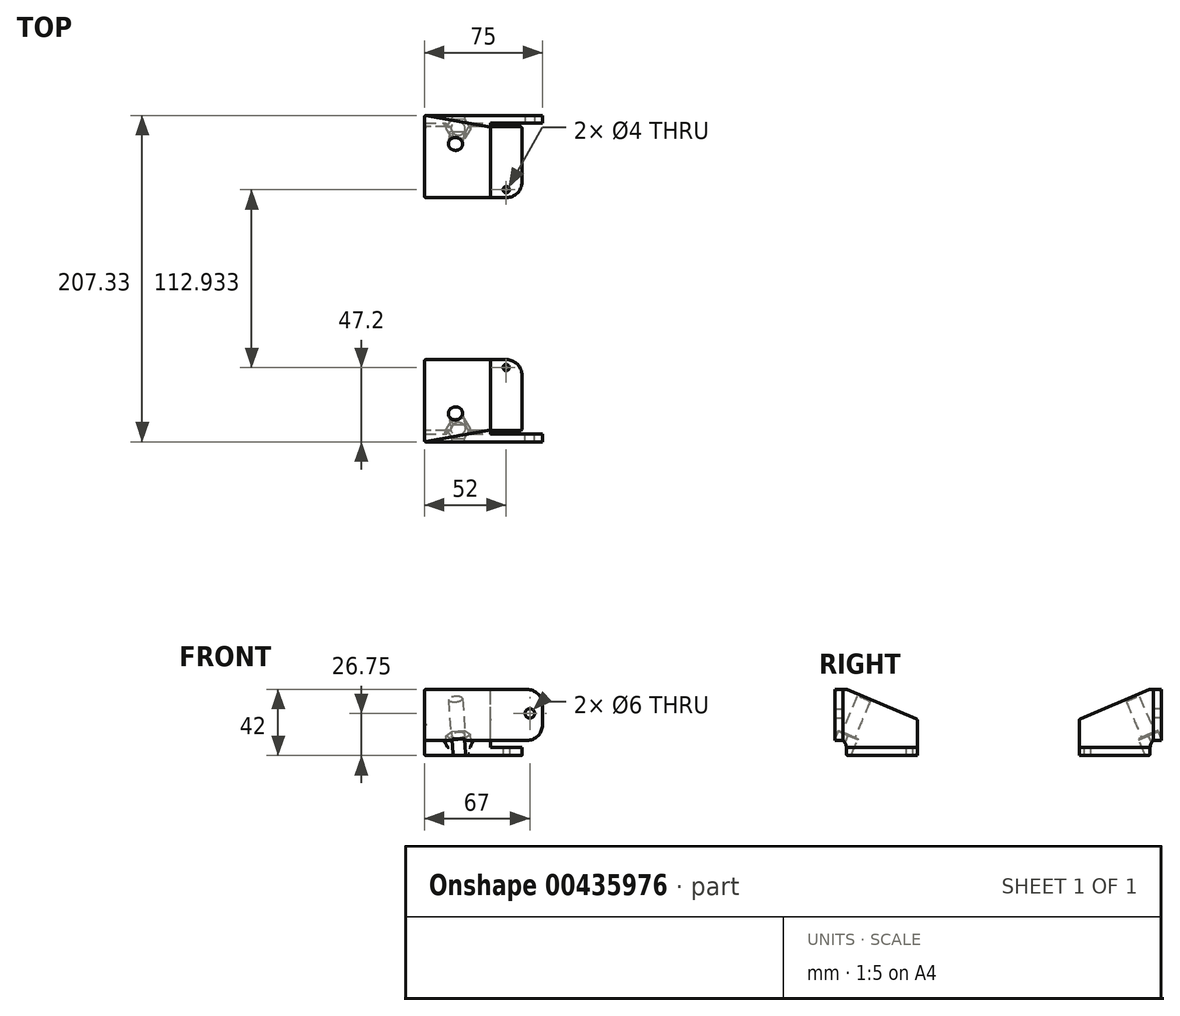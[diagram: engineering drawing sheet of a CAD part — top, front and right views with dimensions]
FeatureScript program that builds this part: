
annotation { "Feature Type Name" : "Feature", "Feature Type Description" : "" }
export const myFeature = defineFeature(function(context is Context, id is Id, definition is map)
    precondition{}
    {
        {
            var Q0;
            Q0=qCreatedBy(makeId("Top.planeOp"),FACE);
            var sketch = newSketch(context, id + "F0", { "sketchPlane" : qUnion([Q0])});
            skLineSegment(sketch, "E0.bottom", {"start": v(10, -22.5) * mm, "end": v(-10, -22.5) * mm});
            skLineSegment(sketch, "E0.top", {"start": v(10, 22.5) * mm, "end": v(-10, 22.5) * mm});
            skLineSegment(sketch, "E0.left", {"start": v(10, -22.5) * mm, "end": v(10, 22.5) * mm});
            skLineSegment(sketch, "E0.right", {"start": v(-10, -22.5) * mm, "end": v(-10, 22.5) * mm});
            skPoint(sketch, "E0.middle", {"position": v(0, 0) * mm});
            skCircle(sketch, "E1", {"center": v(0, 17.5) * mm, "radius": 2 * mm});
            skSolve(sketch);
        }
        {
            var Q0;
            Q0=makeQuery(id+"F0.imprint","IMPRINT",FACE,{"disambiguationData":[TD([[makeQuery(id+"F0.imprint","IMPRINT",EDGE,{"derivedFrom":sQuery(id+"F0.wireOp",EDGE,"E0.bottom")}),-1.0]])]});
            extrude(context, id + "F1", {"entities" : qUnion([Q0]), "depth" : 5 * mm});
        }
        {
            var Q0;
            Q0=makeQuery(id+"F1.opExtrude","SWEPT_FACE",FACE,{"disambiguationData":[OSD([sQuery(id+"F0.wireOp",EDGE,"E0.right")])]});
            var sketch = newSketch(context, id + "F2", { "sketchPlane" : qUnion([Q0])});
            skPoint(sketch, "E2.0", {"position": v(-22.5, 0) * mm});
            skLineSegment(sketch, "E3.bottom", {"start": v(-22.5, 0) * mm, "end": v(22.5, 0) * mm});
            skLineSegment(sketch, "E3.top", {"start": v(-22.5, 42) * mm, "end": v(22.5, 42) * mm});
            skLineSegment(sketch, "E3.left", {"start": v(-22.5, 0) * mm, "end": v(-22.5, 42) * mm});
            skLineSegment(sketch, "E3.right", {"start": v(22.5, 0) * mm, "end": v(22.5, 42) * mm});
            skSolve(sketch);
        }
        {
            var Q0;
            {var subQ0=sQuery(id+"F2.wireOp",EDGE,"E3.top");Q0=makeQuery(id+"F2.imprint","IMPRINT",FACE,{"disambiguationData":[TD([[makeQuery(id+"F2.imprint","IMPRINT",EDGE,{"derivedFrom":subQ0}),-1.0]])]});}
            var Q1;
            {var subQ0=sQuery(id+"F2.wireOp",EDGE,"E3.bottom");Q1=makeQuery(id+"F2.imprint","IMPRINT",FACE,{"disambiguationData":[TD([[makeQuery(id+"F2.imprint","IMPRINT",EDGE,{"derivedFrom":subQ0}),-1.0]])]});}
            extrude(context, id + "F3", {"entities" : qUnion([Q0, Q1]), "operationType" : NewBodyOperationType.ADD, "depth" : 42 * mm});
        }
        {
            var Q0;
            Q0=makeQuery(id+"F3.boolean.opBoolean","MERGE",FACE,{"derivedFrom":[makeQuery(id+"F1.opExtrude","SWEPT_FACE",FACE,{"disambiguationData":[OSD([sQuery(id+"F0.wireOp",EDGE,"E0.bottom")])]}),makeQuery(id+"F3.opExtrude","SWEPT_FACE",FACE,{"disambiguationData":[OSD([sQuery(id+"F2.wireOp",EDGE,"E3.right")])]})]});
            var sketch = newSketch(context, id + "F4", { "sketchPlane" : qUnion([Q0])});
            skPoint(sketch, "E4.0", {"position": v(-10, 5) * mm});
            skLineSegment(sketch, "E5.bottom", {"start": v(-10, 5) * mm, "end": v(-52, 5) * mm});
            skLineSegment(sketch, "E5.top", {"start": v(-10, 42) * mm, "end": v(-52, 42) * mm});
            skLineSegment(sketch, "E5.left", {"start": v(-10, 5) * mm, "end": v(-10, 42) * mm});
            skLineSegment(sketch, "E5.right", {"start": v(-52, 5) * mm, "end": v(-52, 42) * mm});
            skSolve(sketch);
        }
        {
            var Q0;
            Q0=makeQuery(id+"F4.imprint","IMPRINT",FACE,{"disambiguationData":[TD([[makeQuery(id+"F4.imprint","IMPRINT",EDGE,{"derivedFrom":sQuery(id+"F4.wireOp",EDGE,"E5.bottom")}),-1.0]])]});
            extrude(context, id + "F5", {"entities" : qUnion([Q0]), "operationType" : NewBodyOperationType.ADD, "depth" : 2.2 * mm});
        }
        {
            var Q0;
            Q0=makeQuery(id+"F5.opExtrude","CAP_FACE",FACE,{"disambiguationData":[OSD([sQuery(id+"F4.wireOp",EDGE,"E5.bottom"),sQuery(id+"F4.wireOp",EDGE,"E5.top"),sQuery(id+"F4.wireOp",EDGE,"E5.left"),sQuery(id+"F4.wireOp",EDGE,"E5.right")])],"isStart":false});
            var sketch = newSketch(context, id + "F6", { "sketchPlane" : qUnion([Q0])});
            skPoint(sketch, "E6.0", {"position": v(-10, 5) * mm});
            skPoint(sketch, "E7.0", {"position": v(-52, 42) * mm});
            skPoint(sketch, "E8.0", {"position": v(10, 5) * mm});
            skLineSegment(sketch, "E9.bottom", {"start": v(-52, 42) * mm, "end": v(23, 42) * mm});
            skLineSegment(sketch, "E9.top", {"start": v(-52, 9.55) * mm, "end": v(23, 9.55) * mm});
            skLineSegment(sketch, "E9.left", {"start": v(-52, 42) * mm, "end": v(-52, 9.55) * mm});
            skLineSegment(sketch, "E9.right", {"start": v(23, 42) * mm, "end": v(23, 9.55) * mm});
            skLineSegment(sketch, "E10", {"start": v(15, 9.55) * mm, "end": v(15, 42) * mm, "construction": true});
            skLineSegment(sketch, "E11", {"start": v(-10, 5) * mm, "end": v(-10, 26.75) * mm, "construction": true});
            skCircle(sketch, "E12", {"center": v(15, 26.75) * mm, "radius": 3 * mm});
            skSolve(sketch);
        }
        {
            var Q0;
            {var subQ3=sQuery(id+"F6.wireOp",EDGE,"E9.left");Q0=makeQuery(id+"F6.imprint","IMPRINT",FACE,{"disambiguationData":[TD([[makeQuery(id+"F6.imprint","IMPRINT",EDGE,{"derivedFrom":subQ3}),-1.0]])]});}
            var Q1;
            {var subQ3=sQuery(id+"F6.wireOp",EDGE,"E9.right");Q1=makeQuery(id+"F6.imprint","IMPRINT",FACE,{"disambiguationData":[TD([[makeQuery(id+"F6.imprint","IMPRINT",EDGE,{"derivedFrom":subQ3}),-1.0]])]});}
            extrude(context, id + "F7", {"entities" : qUnion([Q0, Q1]), "operationType" : NewBodyOperationType.ADD, "depth" : 5 * mm});
        }
        {
            var Q0;
            Q0=qCreatedBy(makeId("Right.planeOp"),FACE);
            var sketch = newSketch(context, id + "F8", { "sketchPlane" : qUnion([Q0])});
            skLineSegment(sketch, "E13", {"start": v(0, 0) * mm, "end": v(-80.94, 34.36) * mm, "construction": true});
            skSolve(sketch);
        }
        {
            var Q0;
            Q0=sQuery(id+"F8.wireOp",EDGE,"E13");
            cPlane(context, id + "F9", {"entities" : qUnion([Q0]), "cplaneType" : CPlaneType.LINE_ANGLE, "offset" : 25 * mm, "angle" : 0 * degree, "width" : 150 * mm, "height" : 150 * mm});
        }
        {
            var Q0;
            Q0=qCreatedBy(id+"F9.planeOp",FACE);
            var sketch = newSketch(context, id + "F10", { "sketchPlane" : qUnion([Q0])});
            skLineSegment(sketch, "E14", {"start": v(-52.7, -8.91) * mm, "end": v(-52.7, 97.33) * mm, "construction": true});
            skSolve(sketch);
        }
        {
            var Q0;
            Q0=sQuery(id+"F10.wireOp",EDGE,"E14");
            cPlane(context, id + "F11", {"entities" : qUnion([Q0]), "cplaneType" : CPlaneType.LINE_ANGLE, "offset" : 25 * mm, "angle" : 4 * degree, "width" : 150 * mm, "height" : 150 * mm});
        }
        {
            var Q0;
            Q0=qCreatedBy(id+"F11.planeOp",FACE);
            var sketch = newSketch(context, id + "F12", { "sketchPlane" : qUnion([Q0])});
            skPoint(sketch, "E15.0", {"position": v(-52.23, 24.7) * mm});
            skPoint(sketch, "E16.0", {"position": v(-10.33, 24.7) * mm});
            skPoint(sketch, "E17.0.midPoint", {"position": v(-25.67, 24.7) * mm});
            skCircle(sketch, "E18", {"center": v(-30.23, 24.7) * mm, "radius": 4.5 * mm});
            skCircle(sketch, "E19.cCircle", {"center": v(-30.23, 24.7) * mm, "radius": 6.75 * mm, "construction": true});
            skLineSegment(sketch, "E19.0", {"start": v(-26.33, 17.94) * mm, "end": v(-34.12, 17.94) * mm});
            skLineSegment(sketch, "E19.1", {"start": v(-34.12, 17.94) * mm, "end": v(-38.02, 24.7) * mm});
            skLineSegment(sketch, "E19.2", {"start": v(-38.02, 24.7) * mm, "end": v(-34.12, 31.44) * mm});
            skLineSegment(sketch, "E19.3", {"start": v(-34.12, 31.44) * mm, "end": v(-26.33, 31.44) * mm});
            skLineSegment(sketch, "E19.4", {"start": v(-26.33, 31.44) * mm, "end": v(-22.43, 24.7) * mm});
            skLineSegment(sketch, "E19.5", {"start": v(-22.43, 24.7) * mm, "end": v(-26.33, 17.94) * mm});
            skPoint(sketch, "E19.0.midPoint", {"position": v(-30.23, 17.94) * mm});
            skSolve(sketch);
        }
        {
            var Q0;
            Q0=makeQuery(id+"F12.imprint","IMPRINT",FACE,{"disambiguationData":[TD([[makeQuery(id+"F12.imprint","IMPRINT",EDGE,{"derivedFrom":sQuery(id+"F12.wireOp",EDGE,"E18")}),1.0]])]});
            extrude(context, id + "F13", {"entities" : qUnion([Q0]), "operationType" : NewBodyOperationType.REMOVE, "endBound" : BoundingType.THROUGH_ALL, "oppositeDirection" : true, "depth" : 25 * mm, "hasSecondDirection" : true, "secondDirectionBound" : SecondDirectionBoundingType.THROUGH_ALL, "secondDirectionOppositeDirection" : false, "secondDirectionDepth" : 25 * mm});
        }
        {
            var Q0;
            Q0=makeQuery(id+"F12.imprint","IMPRINT",FACE,{"disambiguationData":[TD([[makeQuery(id+"F12.imprint","IMPRINT",EDGE,{"derivedFrom":sQuery(id+"F12.wireOp",EDGE,"E18")}),-1.0]])]});
            extrude(context, id + "F14", {"entities" : qUnion([Q0]), "operationType" : NewBodyOperationType.REMOVE, "endBound" : BoundingType.THROUGH_ALL, "depth" : 10 * mm, "hasSecondDirection" : true, "secondDirectionOppositeDirection" : true, "secondDirectionDepth" : 2 * mm});
        }
        {
            var Q0;
            Q0=qCreatedBy(id+"F11.planeOp",FACE);
            cPlane(context, id + "F15", {"entities" : qUnion([Q0]), "cplaneType" : CPlaneType.OFFSET, "offset" : 30.5 * mm, "oppositeDirection" : true, "width" : 150 * mm, "height" : 150 * mm});
        }
        {
            var Q0;
            Q0=qCreatedBy(id+"F15.planeOp",FACE);
            var sketch = newSketch(context, id + "F16", { "sketchPlane" : qUnion([Q0])});
            skLineSegment(sketch, "E20", {"start": v(8.4, 62.06) * mm, "end": v(8.4, -46.08) * mm});
            skLineSegment(sketch, "E21", {"start": v(8.4, -46.08) * mm, "end": v(-61.42, -46.22) * mm});
            skLineSegment(sketch, "E22", {"start": v(-61.42, -46.22) * mm, "end": v(-61.64, 62.06) * mm});
            skLineSegment(sketch, "E23", {"start": v(8.4, 62.06) * mm, "end": v(-61.64, 62.06) * mm});
            skSolve(sketch);
        }
        {
            var Q0;
            Q0=makeQuery(id+"F16.imprint","IMPRINT",FACE,{"disambiguationData":[TD([[makeQuery(id+"F16.imprint","IMPRINT",EDGE,{"derivedFrom":sQuery(id+"F16.wireOp",EDGE,"E20")}),-1.0]])]});
            extrude(context, id + "F17", {"entities" : qUnion([Q0]), "operationType" : NewBodyOperationType.REMOVE, "depth" : 3.55 * mm, "hasSecondDirection" : true, "secondDirectionOppositeDirection" : true, "secondDirectionDepth" : 25 * mm});
        }
        {
            var Q0;
            Q0=makeQuery(id+"F7.boolean.opBoolean","MERGE",FACE,{"derivedFrom":[makeQuery(id+"F5.boolean.opBoolean","MERGE",FACE,{"derivedFrom":[makeQuery(id+"F3.opExtrude","CAP_FACE",FACE,{"disambiguationData":[OSD([sQuery(id+"F2.wireOp",EDGE,"E3.bottom"),sQuery(id+"F2.wireOp",EDGE,"E3.top"),sQuery(id+"F2.wireOp",EDGE,"E3.left"),sQuery(id+"F2.wireOp",EDGE,"E3.right")])],"isStart":false}),makeQuery(id+"F5.opExtrude","SWEPT_FACE",FACE,{"disambiguationData":[OSD([sQuery(id+"F4.wireOp",EDGE,"E5.right")])]})]}),makeQuery(id+"F7.opExtrude","SWEPT_FACE",FACE,{"disambiguationData":[OSD([sQuery(id+"F6.wireOp",EDGE,"E9.left")])]})]});
            var sketch = newSketch(context, id + "F18", { "sketchPlane" : qUnion([Q0])});
            skArc(sketch, "E24", {"start": v(24.7, 9.55) * mm, "mid": v(23.08, 7.53) * mm, "end": v(22.5, 5) * mm});
            skLineSegment(sketch, "E25", {"start": v(24.7, 9.55) * mm, "end": v(24.7, 5) * mm});
            skLineSegment(sketch, "E26", {"start": v(24.7, 5) * mm, "end": v(22.5, 5) * mm});
            skSolve(sketch);
        }
        {
            var Q0;
            Q0=makeQuery(id+"F18.imprint","IMPRINT",FACE,{"disambiguationData":[TD([[makeQuery(id+"F18.imprint","IMPRINT",EDGE,{"derivedFrom":sQuery(id+"F18.wireOp",EDGE,"E24")}),1.0]])]});
            extrude(context, id + "F19", {"entities" : qUnion([Q0]), "operationType" : NewBodyOperationType.REMOVE, "endBound" : BoundingType.THROUGH_ALL, "oppositeDirection" : true, "depth" : 25 * mm});
        }
        {
            var Q0;
            Q0=makeQuery(id+"F7.opExtrude","SWEPT_EDGE",EDGE,{"disambiguationData":[OSD([sQuery(id+"F6.wireOp",EDGE,"E9.bottom"),sQuery(id+"F6.wireOp",EDGE,"E9.right")])]});
            var Q1;
            Q1=makeQuery(id+"F7.opExtrude","SWEPT_EDGE",EDGE,{"disambiguationData":[OSD([sQuery(id+"F6.wireOp",EDGE,"E9.top"),sQuery(id+"F6.wireOp",EDGE,"E9.right")])]});
            var Q2;
            Q2=makeQuery(id+"F1.opExtrude","SWEPT_EDGE",EDGE,{"disambiguationData":[OSD([sQuery(id+"F0.wireOp",EDGE,"E0.top"),sQuery(id+"F0.wireOp",EDGE,"E0.left")])]});
            fillet(context, id + "F20", {"entities" : qUnion([Q0, Q1, Q2]), "radius" : 10 * mm, "tangentPropagation" : true, "allowEdgeOverflow" : false});
        }
        {
            var Q0;
            Q0=makeQuery(id+"F17.boolean.opBoolean","INTERSECT",EDGE,{"derivedFrom":[makeQuery(id+"F3.boolean.opBoolean","MERGE",FACE,{"derivedFrom":[makeQuery(id+"F1.opExtrude","SWEPT_FACE",FACE,{"disambiguationData":[OSD([sQuery(id+"F0.wireOp",EDGE,"E0.top")])]}),makeQuery(id+"F3.opExtrude","SWEPT_FACE",FACE,{"disambiguationData":[OSD([sQuery(id+"F2.wireOp",EDGE,"E3.left")])]})]}),makeQuery(id+"F17.opExtrude","CAP_FACE",FACE,{"disambiguationData":[OSD([sQuery(id+"F16.wireOp",EDGE,"E20"),sQuery(id+"F16.wireOp",EDGE,"E21"),sQuery(id+"F16.wireOp",EDGE,"E22"),sQuery(id+"F16.wireOp",EDGE,"E23")])],"isStart":false})]});
            var Q1;
            Q1=makeQuery(id+"F17.boolean.opBoolean","INTERSECT",EDGE,{"derivedFrom":[makeQuery(id+"F7.boolean.opBoolean","MERGE",FACE,{"derivedFrom":[makeQuery(id+"F5.boolean.opBoolean","MERGE",FACE,{"derivedFrom":[makeQuery(id+"F3.opExtrude","CAP_FACE",FACE,{"disambiguationData":[OSD([sQuery(id+"F2.wireOp",EDGE,"E3.bottom"),sQuery(id+"F2.wireOp",EDGE,"E3.top"),sQuery(id+"F2.wireOp",EDGE,"E3.left"),sQuery(id+"F2.wireOp",EDGE,"E3.right")])],"isStart":false}),makeQuery(id+"F5.opExtrude","SWEPT_FACE",FACE,{"disambiguationData":[OSD([sQuery(id+"F4.wireOp",EDGE,"E5.right")])]})]}),makeQuery(id+"F7.opExtrude","SWEPT_FACE",FACE,{"disambiguationData":[OSD([sQuery(id+"F6.wireOp",EDGE,"E9.left")])]})]}),makeQuery(id+"F17.opExtrude","CAP_FACE",FACE,{"disambiguationData":[OSD([sQuery(id+"F16.wireOp",EDGE,"E20"),sQuery(id+"F16.wireOp",EDGE,"E21"),sQuery(id+"F16.wireOp",EDGE,"E22"),sQuery(id+"F16.wireOp",EDGE,"E23")])],"isStart":false})]});
            var Q2;
            Q2=makeQuery(id+"F3.opExtrude","CAP_EDGE",EDGE,{"disambiguationData":[OSD([sQuery(id+"F2.wireOp",EDGE,"E3.left")])],"isStart":false});
            var Q3;
            Q3=makeQuery(id+"F3.opExtrude","CAP_EDGE",EDGE,{"disambiguationData":[OSD([sQuery(id+"F2.wireOp",EDGE,"E3.bottom")])],"isStart":false});
            var Q4;
            Q4=makeQuery(id+"F7.opExtrude","CAP_EDGE",EDGE,{"disambiguationData":[OSD([sQuery(id+"F6.wireOp",EDGE,"E9.left")])],"isStart":false});
            var Q5;
            {var subQ0=sQuery(id+"F2.wireOp",EDGE,"E3.bottom");var subQ1=sQuery(id+"F0.wireOp",EDGE,"E0.bottom");var subQ2=sQuery(id+"F2.wireOp",EDGE,"E3.right");Q5=makeQuery(id+"F13.boolean.opBoolean","SPLIT",EDGE,{"disambiguationData":[TD([makeQuery(id+"F5.opExtrude","SWEPT_FACE",FACE,{"disambiguationData":[OSD([sQuery(id+"F4.wireOp",EDGE,"E5.right")])]})])],"derivedFrom":makeQuery(id+"F3.boolean.opBoolean","MERGE",EDGE,{"derivedFrom":[makeQuery(id+"F1.opExtrude","CAP_EDGE",EDGE,{"disambiguationData":[OSD([subQ1])],"isStart":true}),makeQuery(id+"F3.opExtrude","SWEPT_EDGE",EDGE,{"disambiguationData":[OSD([subQ0,subQ2])]})]})});}
            var Q6;
            {var subQ0=sQuery(id+"F2.wireOp",EDGE,"E3.bottom");var subQ1=sQuery(id+"F0.wireOp",EDGE,"E0.left");var subQ2=sQuery(id+"F0.wireOp",EDGE,"E0.bottom");var subQ3=sQuery(id+"F2.wireOp",EDGE,"E3.right");Q6=makeQuery(id+"F13.boolean.opBoolean","SPLIT",EDGE,{"disambiguationData":[TD([makeQuery(id+"F1.opExtrude","SWEPT_FACE",FACE,{"disambiguationData":[OSD([subQ1])]})])],"derivedFrom":makeQuery(id+"F3.boolean.opBoolean","MERGE",EDGE,{"derivedFrom":[makeQuery(id+"F1.opExtrude","CAP_EDGE",EDGE,{"disambiguationData":[OSD([subQ2])],"isStart":true}),makeQuery(id+"F3.opExtrude","SWEPT_EDGE",EDGE,{"disambiguationData":[OSD([subQ0,subQ3])]})]})});}
            var Q7;
            Q7=makeQuery(id+"F14.boolean.opBoolean","INTERSECT",EDGE,{"derivedFrom":[makeQuery(id+"F3.boolean.opBoolean","MERGE",FACE,{"derivedFrom":[makeQuery(id+"F1.opExtrude","CAP_FACE",FACE,{"disambiguationData":[OSD([sQuery(id+"F0.wireOp",EDGE,"E0.bottom"),sQuery(id+"F0.wireOp",EDGE,"E0.top"),sQuery(id+"F0.wireOp",EDGE,"E0.left"),sQuery(id+"F0.wireOp",EDGE,"E0.right"),sQuery(id+"F0.wireOp",EDGE,"E1")])],"isStart":true}),makeQuery(id+"F3.opExtrude","SWEPT_FACE",FACE,{"disambiguationData":[OSD([sQuery(id+"F2.wireOp",EDGE,"E3.bottom")])]})]}),makeQuery(id+"F14.opExtrude","SWEPT_FACE",FACE,{"disambiguationData":[OSD([sQuery(id+"F12.wireOp",EDGE,"E19.1")])]})]});
            var Q8;
            Q8=makeQuery(id+"F14.boolean.opBoolean","INTERSECT",EDGE,{"derivedFrom":[makeQuery(id+"F3.boolean.opBoolean","MERGE",FACE,{"derivedFrom":[makeQuery(id+"F1.opExtrude","CAP_FACE",FACE,{"disambiguationData":[OSD([sQuery(id+"F0.wireOp",EDGE,"E0.bottom"),sQuery(id+"F0.wireOp",EDGE,"E0.top"),sQuery(id+"F0.wireOp",EDGE,"E0.left"),sQuery(id+"F0.wireOp",EDGE,"E0.right"),sQuery(id+"F0.wireOp",EDGE,"E1")])],"isStart":true}),makeQuery(id+"F3.opExtrude","SWEPT_FACE",FACE,{"disambiguationData":[OSD([sQuery(id+"F2.wireOp",EDGE,"E3.bottom")])]})]}),makeQuery(id+"F14.opExtrude","SWEPT_FACE",FACE,{"disambiguationData":[OSD([sQuery(id+"F12.wireOp",EDGE,"E19.0")])]})]});
            var Q9;
            Q9=makeQuery(id+"F14.boolean.opBoolean","INTERSECT",EDGE,{"derivedFrom":[makeQuery(id+"F3.boolean.opBoolean","MERGE",FACE,{"derivedFrom":[makeQuery(id+"F1.opExtrude","CAP_FACE",FACE,{"disambiguationData":[OSD([sQuery(id+"F0.wireOp",EDGE,"E0.bottom"),sQuery(id+"F0.wireOp",EDGE,"E0.top"),sQuery(id+"F0.wireOp",EDGE,"E0.left"),sQuery(id+"F0.wireOp",EDGE,"E0.right"),sQuery(id+"F0.wireOp",EDGE,"E1")])],"isStart":true}),makeQuery(id+"F3.opExtrude","SWEPT_FACE",FACE,{"disambiguationData":[OSD([sQuery(id+"F2.wireOp",EDGE,"E3.bottom")])]})]}),makeQuery(id+"F14.opExtrude","SWEPT_FACE",FACE,{"disambiguationData":[OSD([sQuery(id+"F12.wireOp",EDGE,"E19.5")])]})]});
            var Q10;
            {var subQ3=sQuery(id+"F0.wireOp",EDGE,"E0.left");var subQ5=sQuery(id+"F0.wireOp",EDGE,"E0.bottom");var subQ6=sQuery(id+"F2.wireOp",EDGE,"E3.right");Q10=makeQuery(id+"F14.boolean.opBoolean","INTERSECT",EDGE,{"derivedFrom":[makeQuery(id+"F13.boolean.opBoolean","SPLIT",FACE,{"disambiguationData":[TD([makeQuery(id+"F1.opExtrude","SWEPT_FACE",FACE,{"disambiguationData":[OSD([subQ3])]})])],"derivedFrom":makeQuery(id+"F3.boolean.opBoolean","MERGE",FACE,{"derivedFrom":[makeQuery(id+"F1.opExtrude","SWEPT_FACE",FACE,{"disambiguationData":[OSD([subQ5])]}),makeQuery(id+"F3.opExtrude","SWEPT_FACE",FACE,{"disambiguationData":[OSD([subQ6])]})]})}),makeQuery(id+"F14.opExtrude","SWEPT_FACE",FACE,{"disambiguationData":[OSD([sQuery(id+"F12.wireOp",EDGE,"E19.5")])]})]});}
            var Q11;
            Q11=makeQuery(id+"F19.boolean.opBoolean","INTERSECT",EDGE,{"derivedFrom":[makeQuery(id+"F14.boolean.opBoolean","COPY",FACE,{"derivedFrom":makeQuery(id+"F14.opExtrude","SWEPT_FACE",FACE,{"disambiguationData":[OSD([sQuery(id+"F12.wireOp",EDGE,"E19.5")])]})}),makeQuery(id+"F19.opExtrude","SWEPT_FACE",FACE,{"disambiguationData":[OSD([sQuery(id+"F18.wireOp",EDGE,"E24")])]})]});
            var Q12;
            Q12=makeQuery(id+"F19.boolean.opBoolean","INTERSECT",EDGE,{"derivedFrom":[makeQuery(id+"F14.boolean.opBoolean","COPY",FACE,{"derivedFrom":makeQuery(id+"F14.opExtrude","SWEPT_FACE",FACE,{"disambiguationData":[OSD([sQuery(id+"F12.wireOp",EDGE,"E19.4")])]})}),makeQuery(id+"F19.opExtrude","SWEPT_FACE",FACE,{"disambiguationData":[OSD([sQuery(id+"F18.wireOp",EDGE,"E24")])]})]});
            var Q13;
            Q13=makeQuery(id+"F14.boolean.opBoolean","INTERSECT",EDGE,{"derivedFrom":[makeQuery(id+"F7.opExtrude","SWEPT_FACE",FACE,{"disambiguationData":[OSD([sQuery(id+"F6.wireOp",EDGE,"E9.top")])]}),makeQuery(id+"F14.opExtrude","SWEPT_FACE",FACE,{"disambiguationData":[OSD([sQuery(id+"F12.wireOp",EDGE,"E19.4")])]})]});
            var Q14;
            {var subQ0=sQuery(id+"F2.wireOp",EDGE,"E3.right");var subQ2=sQuery(id+"F0.wireOp",EDGE,"E0.bottom");Q14=makeQuery(id+"F14.boolean.opBoolean","INTERSECT",EDGE,{"derivedFrom":[makeQuery(id+"F13.boolean.opBoolean","SPLIT",FACE,{"disambiguationData":[TD([makeQuery(id+"F5.opExtrude","SWEPT_FACE",FACE,{"disambiguationData":[OSD([sQuery(id+"F4.wireOp",EDGE,"E5.right")])]})])],"derivedFrom":makeQuery(id+"F3.boolean.opBoolean","MERGE",FACE,{"derivedFrom":[makeQuery(id+"F1.opExtrude","SWEPT_FACE",FACE,{"disambiguationData":[OSD([subQ2])]}),makeQuery(id+"F3.opExtrude","SWEPT_FACE",FACE,{"disambiguationData":[OSD([subQ0])]})]})}),makeQuery(id+"F14.opExtrude","SWEPT_FACE",FACE,{"disambiguationData":[OSD([sQuery(id+"F12.wireOp",EDGE,"E19.1")])]})]});}
            var Q15;
            Q15=makeQuery(id+"F19.boolean.opBoolean","INTERSECT",EDGE,{"derivedFrom":[makeQuery(id+"F14.boolean.opBoolean","COPY",FACE,{"derivedFrom":makeQuery(id+"F14.opExtrude","SWEPT_FACE",FACE,{"disambiguationData":[OSD([sQuery(id+"F12.wireOp",EDGE,"E19.2")])]})}),makeQuery(id+"F19.opExtrude","SWEPT_FACE",FACE,{"disambiguationData":[OSD([sQuery(id+"F18.wireOp",EDGE,"E24")])]})]});
            var Q16;
            Q16=makeQuery(id+"F14.boolean.opBoolean","INTERSECT",EDGE,{"derivedFrom":[makeQuery(id+"F7.opExtrude","SWEPT_FACE",FACE,{"disambiguationData":[OSD([sQuery(id+"F6.wireOp",EDGE,"E9.top")])]}),makeQuery(id+"F14.opExtrude","SWEPT_FACE",FACE,{"disambiguationData":[OSD([sQuery(id+"F12.wireOp",EDGE,"E19.2")])]})]});
            var Q17;
            Q17=makeQuery(id+"F1.opExtrude","SWEPT_EDGE",EDGE,{"disambiguationData":[OSD([sQuery(id+"F0.wireOp",EDGE,"E0.bottom"),sQuery(id+"F0.wireOp",EDGE,"E0.left")])]});
            fillet(context, id + "F21", {"entities" : qUnion([Q0, Q1, Q2, Q3, Q4, Q5, Q6, Q7, Q8, Q9, Q10, Q11, Q12, Q13, Q14, Q15, Q16, Q17]), "radius" : 1 * mm, "tangentPropagation" : true, "allowEdgeOverflow" : false});
        }
        {
            var Q0;
            Q0=qCreatedBy(makeId("Top.planeOp"),FACE);
            var sketch = newSketch(context, id + "F22", { "sketchPlane" : qUnion([Q0])});
            skLineSegment(sketch, "E27", {"start": v(-83.39, 73.97) * mm, "end": v(71.76, 73.97) * mm, "construction": true});
            skSolve(sketch);
        }
        {
            var Q0;
            Q0=sQuery(id+"F22.wireOp",EDGE,"E27");
            cPlane(context, id + "F23", {"entities" : qUnion([Q0]), "cplaneType" : CPlaneType.LINE_ANGLE, "offset" : 25 * mm, "angle" : 0 * degree, "width" : 150 * mm, "height" : 150 * mm});
        }
        {
            var Q0;
            Q0=makeQuery(id+"F1.opExtrude","SWEPT_BODY",BODY,{"disambiguationData":[OSD([sQuery(id+"F0.wireOp",EDGE,"E0.bottom"),sQuery(id+"F0.wireOp",EDGE,"E0.top"),sQuery(id+"F0.wireOp",EDGE,"E0.left"),sQuery(id+"F0.wireOp",EDGE,"E0.right"),sQuery(id+"F0.wireOp",EDGE,"E1")])]});
            var Q1;
            Q1=qCreatedBy(id+"F23.planeOp",FACE);
            mirror(context, id + "F24", {"entities" : qUnion([Q0]), "mirrorPlane" : qUnion([Q1])});
        }
    });
